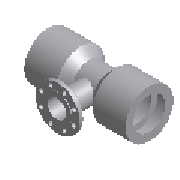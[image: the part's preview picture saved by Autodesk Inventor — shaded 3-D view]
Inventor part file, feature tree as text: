
AUTODESK INVENTOR PART (.ipt)
format: ipt  version: 2023 (Build 270158000, 158)  size: 318,464 bytes
history: native  units: mm (DEFAULTED — no unit token found)
features: other x8, revolve x3, sketch x2, extrude x2, pattern_circular x1
ambient origin geometry x8: Origin, YZ Plane, XZ Plane, XY Plane, X Axis, Y Axis, Z Axis, Center Point
bodies: Solid1 (feature_tree)
feature tree (16):
  sketch  "Sketch1"  dims[d11=156.0mm d0=274.0mm]
  revolve  "Revolve1"  [1 undecoded]
  revolve  "Revolve2"  [1 undecoded]
  sketch  "Sketch2"  dims[d1=383.6mm d2=9.0mm d3=4.5mm d4=109.6mm d5=374.0mm d7=75.0deg d8=9.0mm d9=109.6mm d10=9.0mm d12=270.0mm d123=90.0deg d13=220.0mm d14=118.0mm d15=7.2mm d16=156.0mm d17=140.0mm d18=3.0mm d19=19.0mm d20=15.0deg d132=90.0deg d23=200.0mm d21=0.0mm d22=180.0mm d24=19.0mm d139=200.0mm d25=0.0mm d26=80.0mm d27=360.0deg d144=90.0deg d28=22.5deg d146=100.0mm]
  extrude  "Extrude2"  Depth=4.5mm
  extrude  "Extrude3"  Depth=109.6mm
  pattern_circular  "Circular Pattern1"  [2 undecoded]
  revolve  "Revolve3"  Angle=75.0deg
  other  "Work Point1"
  other  "Work Point2"
  other  "Work Axis1"
  other  "Work Point3"
  other  "Work Axis2"
  other  "Work Point4"
  other  "Work Axis3"
  other  "Work Point5"
note: 4 required parameter values undecoded (feature->parameter linkage not recoverable at this tier; creation-order binding heuristic only, values carry confidence <= 0.55)